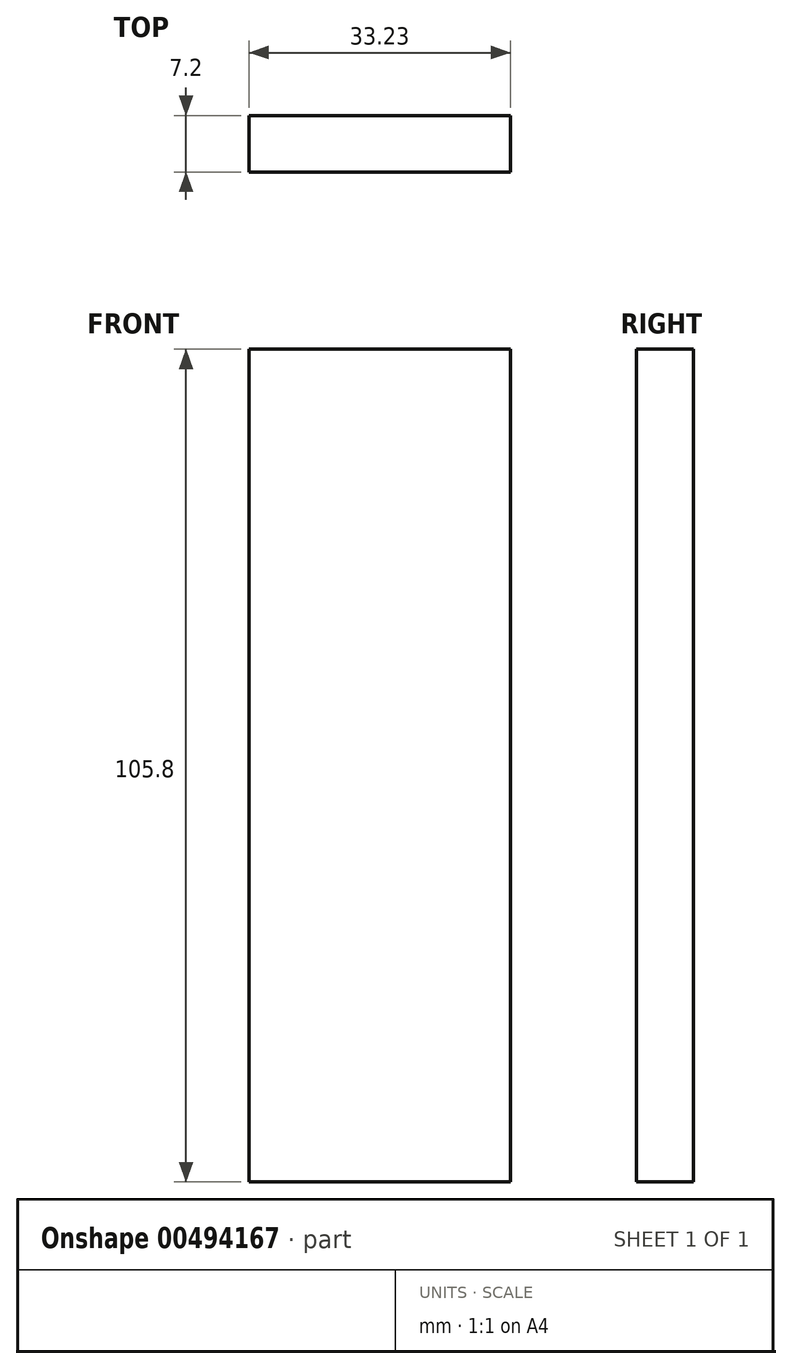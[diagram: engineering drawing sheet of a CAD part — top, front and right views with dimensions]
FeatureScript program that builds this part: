
annotation { "Feature Type Name" : "Feature", "Feature Type Description" : "" }
export const myFeature = defineFeature(function(context is Context, id is Id, definition is map)
    precondition{}
    {
        {
            var Q0;
            Q0=qCreatedBy(makeId("Front.planeOp"),FACE);
            var sketch = newSketch(context, id + "F0", { "sketchPlane" : qUnion([Q0])});
            skLineSegment(sketch, "E0.bottom", {"start": v(-29.44, 47.36) * mm, "end": v(3.79, 47.36) * mm});
            skLineSegment(sketch, "E0.top", {"start": v(-29.44, -58.44) * mm, "end": v(3.79, -58.44) * mm});
            skLineSegment(sketch, "E0.left", {"start": v(-29.44, 47.36) * mm, "end": v(-29.44, -58.44) * mm});
            skLineSegment(sketch, "E0.right", {"start": v(3.79, 47.36) * mm, "end": v(3.79, -58.44) * mm});
            skSolve(sketch);
        }
        {
            var Q0;
            Q0=makeQuery(id+"F0.imprint","IMPRINT",FACE,{"disambiguationData":[TD([[makeQuery(id+"F0.imprint","IMPRINT",EDGE,{"derivedFrom":sQuery(id+"F0.wireOp",EDGE,"E0.bottom")}),-1.0]])]});
            var Q1;
            Q1 = qSketchRegion(id + "F0", true);
            extrude(context, id + "F1", {"entities" : qUnion([Q0, Q1]), "endBound" : BoundingType.SYMMETRIC, "depth" : 7.2 * mm});
        }
    });
